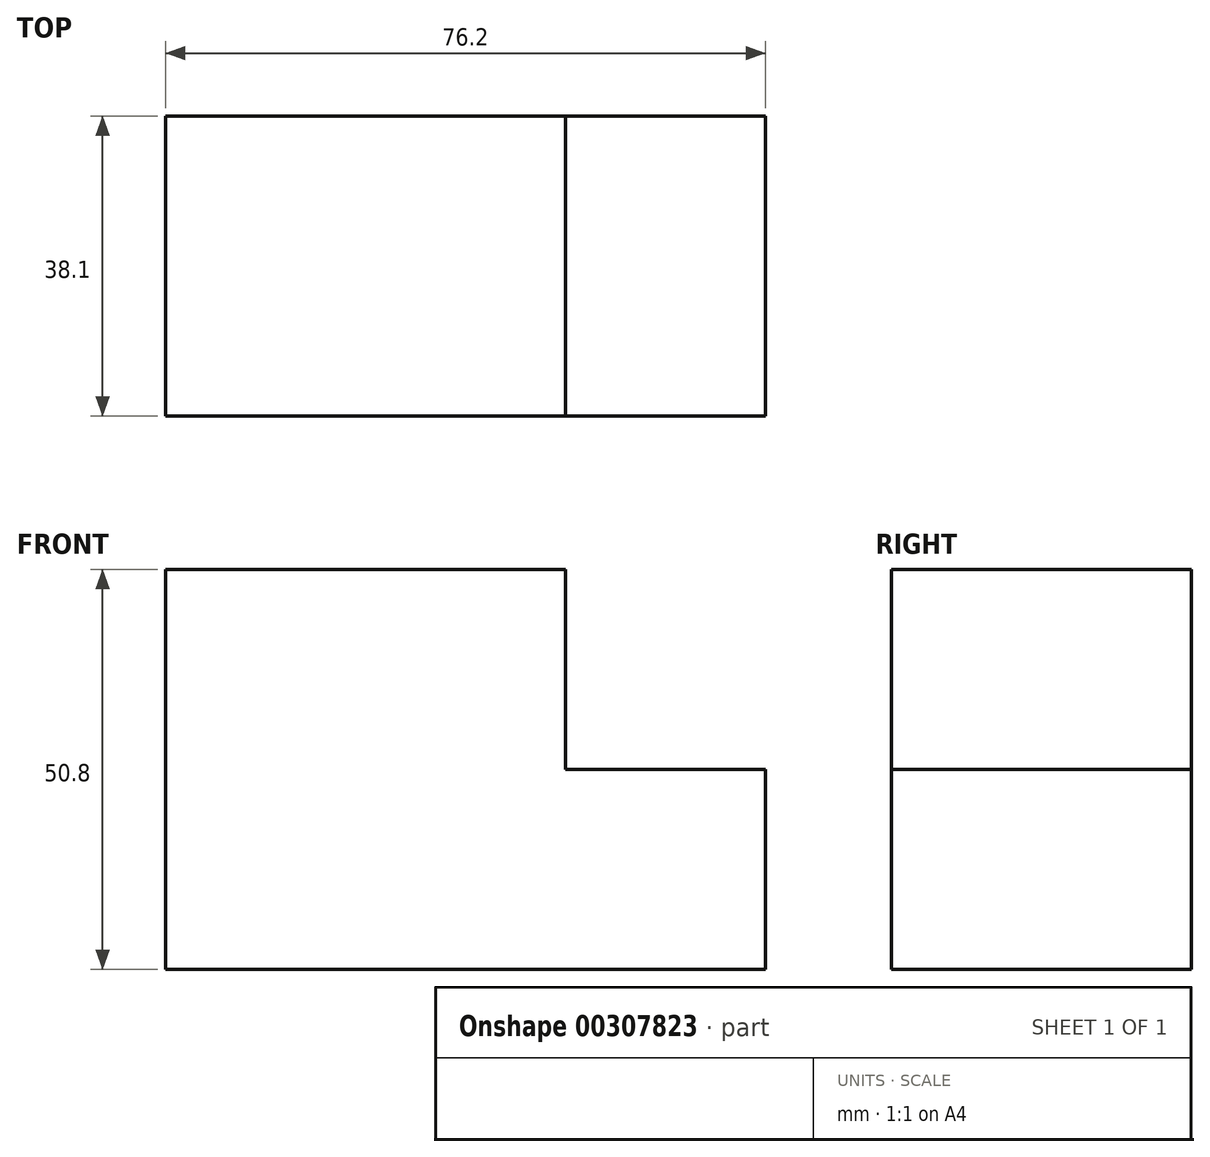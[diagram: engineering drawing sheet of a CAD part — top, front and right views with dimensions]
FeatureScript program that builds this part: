
annotation { "Feature Type Name" : "Feature", "Feature Type Description" : "" }
export const myFeature = defineFeature(function(context is Context, id is Id, definition is map)
    precondition{}
    {
        {
            var Q0;
            Q0=qCreatedBy(makeId("Front.planeOp"),FACE);
            var sketch = newSketch(context, id + "F0", { "sketchPlane" : qUnion([Q0])});
            skLineSegment(sketch, "E0", {"start": v(-37.9, 26.16) * mm, "end": v(12.9, 26.16) * mm});
            skLineSegment(sketch, "E1", {"start": v(12.9, 26.16) * mm, "end": v(12.9, 0.76) * mm});
            skLineSegment(sketch, "E2", {"start": v(12.9, 0.76) * mm, "end": v(38.3, 0.76) * mm});
            skLineSegment(sketch, "E3", {"start": v(38.3, 0.76) * mm, "end": v(38.3, -24.64) * mm});
            skLineSegment(sketch, "E4", {"start": v(38.3, -24.64) * mm, "end": v(-37.9, -24.64) * mm});
            skLineSegment(sketch, "E5", {"start": v(-37.9, -24.64) * mm, "end": v(-37.9, -24.64) * mm});
            skLineSegment(sketch, "E6", {"start": v(-37.9, -24.64) * mm, "end": v(-37.9, 26.16) * mm});
            skSolve(sketch);
        }
        {
            var Q0;
            Q0=makeQuery(id+"F0.imprint","IMPRINT",FACE,{"disambiguationData":[TD([[makeQuery(id+"F0.imprint","IMPRINT",EDGE,{"derivedFrom":sQuery(id+"F0.wireOp",EDGE,"E0")}),-1.0]])]});
            extrude(context, id + "F1", {"entities" : qUnion([Q0]), "depth" : 38.1 * mm});
        }
    });
